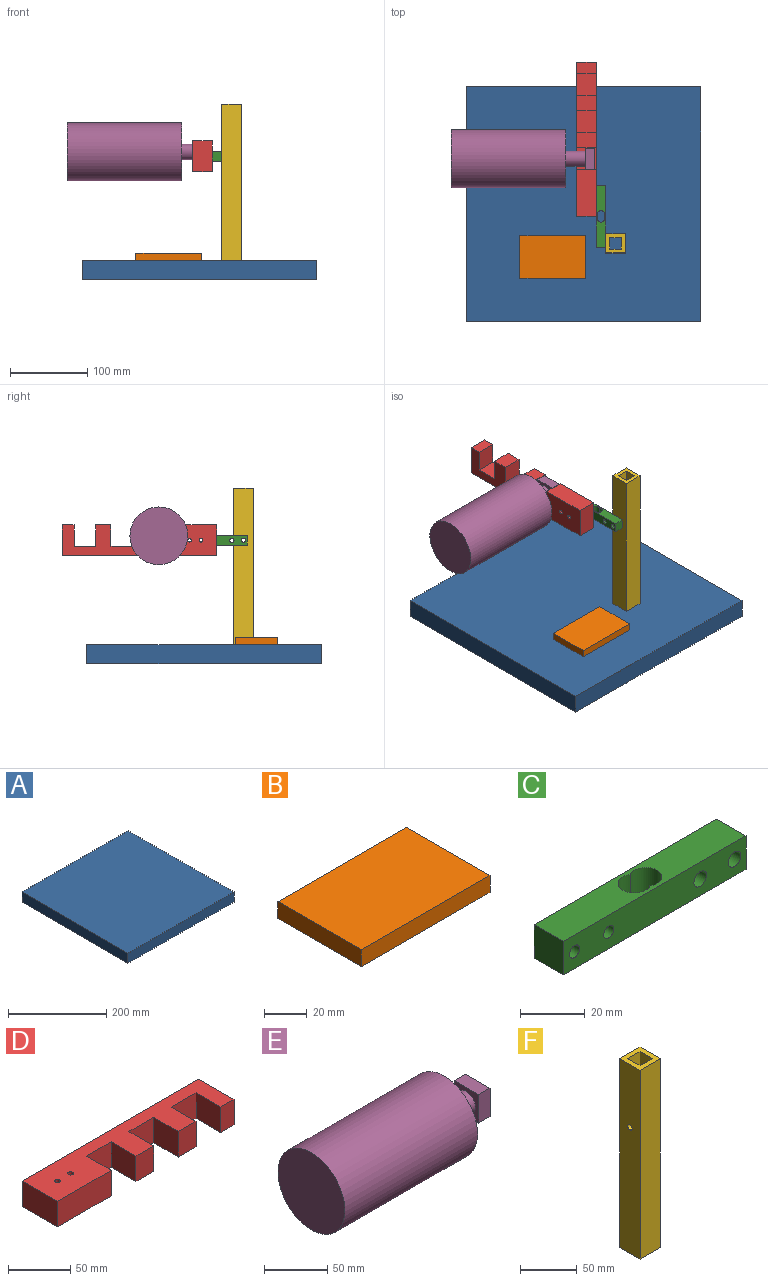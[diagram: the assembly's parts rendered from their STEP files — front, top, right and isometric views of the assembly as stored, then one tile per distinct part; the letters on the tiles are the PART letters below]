
ASSEMBLY  parts=6 mates=5
PART A: 6 faces, bbox 304.8x304.8x25 mm
  f0: plane 304.8x25mm, normal (1,0,0), area 7620mm2, adj f1,f3,f4,f5
  f1: plane 304.8x25mm, normal (0,1,0), area 7620mm2, adj f0,f2,f4,f5
  f2: plane 304.8x25mm, normal (-1,0,0), area 7620mm2, adj f1,f3,f4,f5
  f3: plane 304.8x25mm, normal (0,-1,0), area 7620mm2, adj f0,f2,f4,f5
  f4: plane 304.8x304.8mm, normal (0,0,1), area 92903mm2, adj f0,f1,f2,f3
  f5: plane 304.8x304.8mm, normal (0,0,-1), area 92903mm2, adj f0,f1,f2,f3
PART B: 6 faces, bbox 85x55x9.7 mm
  f0: plane 55x9.7mm, normal (1,0,0), area 533.5mm2, adj f1,f3,f4,f5
  f1: plane 85x9.7mm, normal (0,1,0), area 824.5mm2, adj f0,f2,f4,f5
  f2: plane 55x9.7mm, normal (-1,0,0), area 533.5mm2, adj f1,f3,f4,f5
  f3: plane 85x9.7mm, normal (0,-1,0), area 824.5mm2, adj f0,f2,f4,f5
  f4: plane 85x55mm, normal (0,0,1), area 4675mm2, adj f0,f1,f2,f3
  f5: plane 85x55mm, normal (0,0,-1), area 4675mm2, adj f0,f1,f2,f3
PART C: 12 faces, bbox 80x12.7x12.7 mm
  f0: plane 80x12.7mm, normal (0,0,1), area 889.6mm2, adj f2,f3,f4,f5,f6,f7
  f1: plane 80x12.7mm, normal (0,0,-1), area 889.6mm2, adj f2,f3,f4,f5,f6,f7
  f2: plane 12.7x12.7mm, normal (1,0,0), area 161.3mm2, adj f0,f1,f3,f5
  f3: plane 80x12.7mm, normal (0,1,0), area 936.7mm2, adj f0,f1,f2,f4,f8,f9,f10,f11
  f4: plane 12.7x12.7mm, normal (-1,0,0), area 161.3mm2, adj f0,f1,f3,f5
  f5: plane 80x12.7mm, normal (0,-1,0), area 936.7mm2, adj f0,f1,f2,f4,f8,f9,f10,f11
  f6: cylinder r=5mm len=12.7mm, axis (0,0,1), area 266mm2, adj f0,f1,f7
  f7: cylinder r=5mm len=12.7mm, axis (0,0,1), area 266mm2, adj f0,f1,f6
  f8: cylinder r=2.75mm len=12.7mm, axis (0,-1,0), area 219.4mm2, adj f3,f5
  f9: cylinder r=2.75mm len=12.7mm, axis (0,-1,0), area 219.4mm2, adj f3,f5
  f10: cylinder r=2.25mm len=12.7mm, axis (0,-1,0), area 179.5mm2, adj f3,f5
  f11: cylinder r=2.25mm len=12.7mm, axis (0,-1,0), area 179.5mm2, adj f3,f5
PART D: 20 faces, bbox 200x40x25 mm
  f0: plane 25x20mm, normal (0,-1,0), area 500mm2, adj f3,f4,f13,f15
  f1: plane 25x20mm, normal (0,-1,0), area 500mm2, adj f3,f4,f10,f12
  f2: plane 61x25mm, normal (0,-1,0), area 1525mm2, adj f3,f4,f7,f9
  f3: plane 200x40mm, normal (0,0,1), area 5616.2mm2, adj f0,f1,f2,f5,f6,f7,f8,f9
  f4: plane 200x40mm, normal (0,0,-1), area 5616.2mm2, adj f0,f1,f2,f5,f6,f7,f8,f9
  f5: plane 40x25mm, normal (1,0,0), area 1000mm2, adj f3,f4,f6,f8
  f6: plane 200x25mm, normal (0,1,0), area 5000mm2, adj f3,f4,f5,f7
  f7: plane 40x25mm, normal (-1,0,0), area 1000mm2, adj f2,f3,f4,f6
  f8: plane 25x15mm, normal (0,-1,0), area 375mm2, adj f3,f4,f5,f16
  f9: plane 28x25mm, normal (1,0,0), area 700mm2, adj f2,f3,f4,f11
  f10: plane 28x25mm, normal (-1,0,0), area 700mm2, adj f1,f3,f4,f11
  f11: plane 28x25mm, normal (0,-1,0), area 700mm2, adj f3,f4,f9,f10
  f12: plane 28x25mm, normal (1,0,0), area 700mm2, adj f1,f3,f4,f14
  f13: plane 28x25mm, normal (-1,0,0), area 700mm2, adj f0,f3,f4,f14
  f14: plane 28x25mm, normal (0,-1,0), area 700mm2, adj f3,f4,f12,f13
  f15: plane 28x25mm, normal (1,0,0), area 700mm2, adj f0,f3,f4,f17
  f16: plane 28x25mm, normal (-1,0,0), area 700mm2, adj f3,f4,f8,f17
  f17: plane 28x25mm, normal (0,-1,0), area 700mm2, adj f3,f4,f15,f16
  f18: cylinder r=2.25mm len=25mm, axis (0,0,1), area 353.4mm2, adj f3,f4
  f19: cylinder r=2.25mm len=25mm, axis (0,0,1), area 353.4mm2, adj f3,f4
PART E: 10 faces, bbox 186.7x75x75 mm
  f0: plane 27.5x12.7mm, normal (0,1,0), area 349.2mm2, adj f1,f3,f4,f5
  f1: plane 27.5x12.7mm, normal (0,0,1), area 349.2mm2, adj f0,f2,f4,f5
  f2: plane 27.5x12.7mm, normal (0,-1,0), area 349.2mm2, adj f1,f3,f4,f5
  f3: plane 27.5x12.7mm, normal (0,0,-1), area 349.2mm2, adj f0,f2,f4,f5
  f4: plane 27.5x27.5mm, normal (1,0,0), area 756.2mm2, adj f0,f1,f2,f3
  f5: plane 27.5x27.5mm, normal (-1,0,0), area 442.1mm2, adj f0,f1,f2,f3,f6
  f6: cylinder r=10mm len=25mm, axis (1,0,0), area 1570.8mm2, adj f5,f9
  f7: cylinder r=37.5mm len=149mm, axis (1,0,0), area 35107.3mm2, adj f8,f9
  f8: plane 75x75mm, normal (-1,0,0), area 4417.9mm2, adj f7
  f9: plane 75x75mm, normal (1,0,0), area 4103.7mm2, adj f6,f7
PART F: 12 faces, bbox 25x25x203.2 mm
  f0: plane 203.2x15mm, normal (0,-1,0), area 3048mm2, adj f1,f7,f8,f9
  f1: plane 203.2x15mm, normal (-1,0,0), area 3024.2mm2, adj f0,f2,f8,f9,f11
  f2: plane 203.2x15mm, normal (0,1,0), area 3048mm2, adj f1,f7,f8,f9
  f3: plane 203.2x25mm, normal (1,0,0), area 5056.2mm2, adj f4,f6,f8,f9,f11
  f4: plane 203.2x25mm, normal (0,1,0), area 5080mm2, adj f3,f5,f8,f9
  f5: plane 203.2x25mm, normal (-1,0,0), area 5056.2mm2, adj f4,f6,f8,f9,f10
  f6: plane 203.2x25mm, normal (0,-1,0), area 5080mm2, adj f3,f5,f8,f9
  f7: plane 203.2x15mm, normal (1,0,0), area 3024.2mm2, adj f0,f2,f8,f9,f10
  f8: plane 25x25mm, normal (0,0,1), area 400mm2, adj f0,f1,f2,f3,f4,f5,f6,f7
  f9: plane 25x25mm, normal (0,0,-1), area 400mm2, adj f0,f1,f2,f3,f4,f5,f6,f7
  f10: cylinder r=2.75mm len=5.5mm, axis (1,0,0), area 86.4mm2, adj f5,f7
  f11: cylinder r=2.75mm len=5.5mm, axis (1,0,0), area 86.4mm2, adj f1,f3
PLACE A t=(-0.59,-0.67,-238.97)mm
PLACE B t=(-40.62,-69,-213.97)mm
PLACE C rot(axis=(-0.71,0.71,0),180deg) t=(22.15,-16.73,-72.15)mm
PLACE D rot(axis=(-0.58,-0.58,0.58),120deg) t=(15.8,83.27,-78.5)mm
PLACE E t=(1.51,58.21,-72.75)mm
PLACE F t=(41,-51.73,-213.97)mm
MATE planar E.f3 <-> D.f11  axis (0,0,-1) through (7.86,58.21,-86.5)mm
MATE fastened C.f8 <-> F.f10  axis (1,0,0) through (28.5,-51.73,-78.5)mm
MATE planar B.f5 <-> A.f4  axis (0,0,-1) through (-40.62,-69,-213.97)mm
MATE planar F.f9 <-> A.f4  axis (0,0,-1) through (41,-51.73,-213.97)mm
MATE fastened D.f18 <-> C.f11  axis (1,0,0) through (15.8,18.27,-78.5)mm
